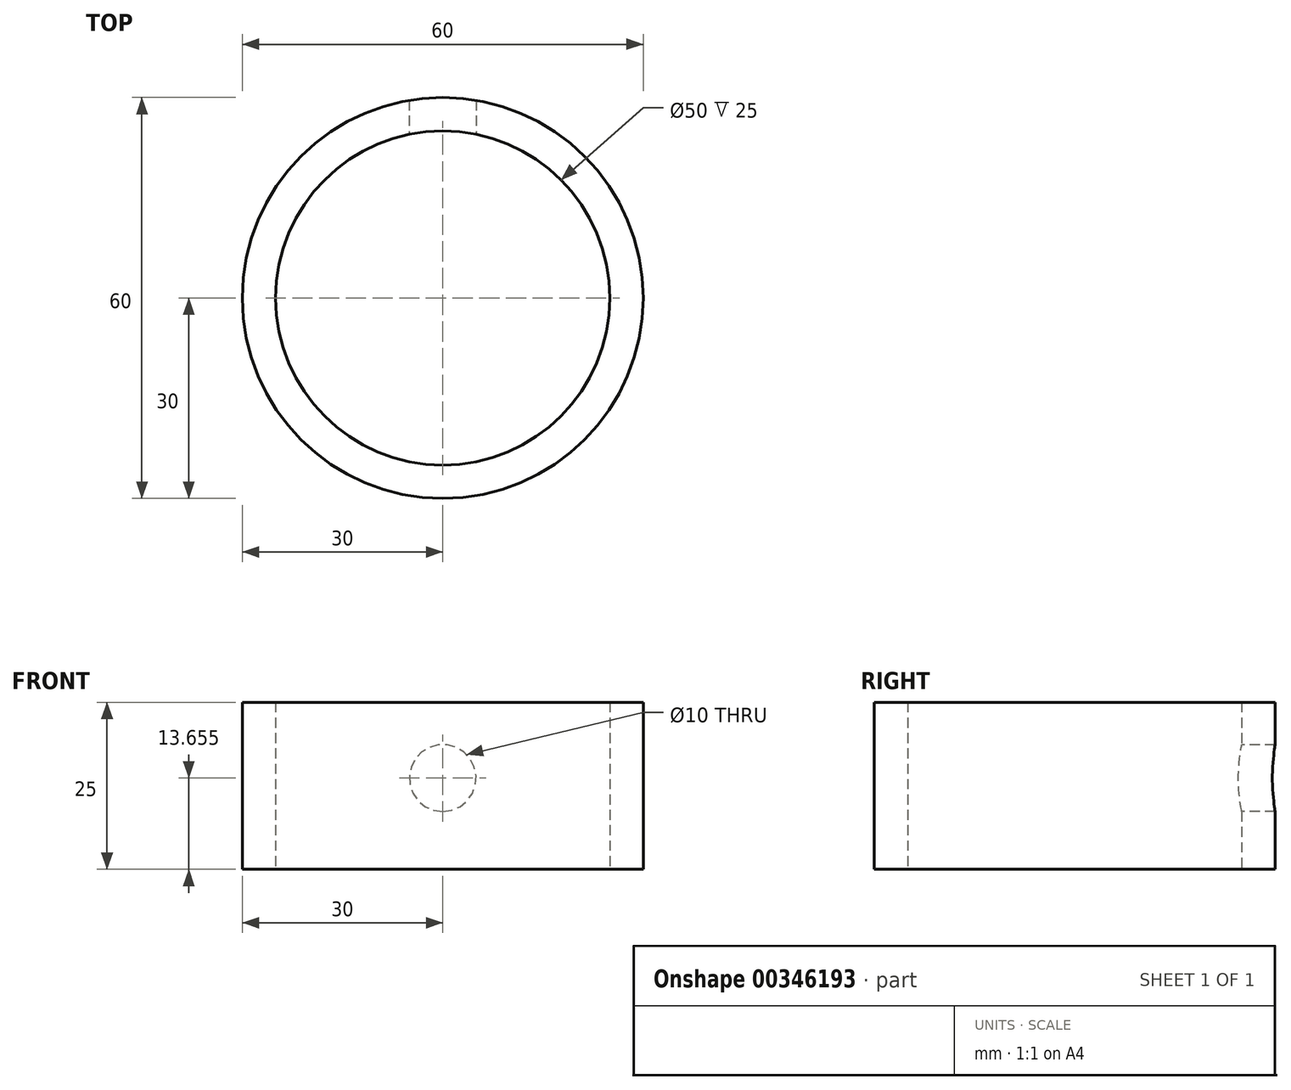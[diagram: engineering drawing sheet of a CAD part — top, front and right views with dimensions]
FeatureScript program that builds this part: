
annotation { "Feature Type Name" : "Feature", "Feature Type Description" : "" }
export const myFeature = defineFeature(function(context is Context, id is Id, definition is map)
    precondition{}
    {
        {
            var Q0;
            Q0=qCreatedBy(makeId("Top.planeOp"),FACE);
            var sketch = newSketch(context, id + "F0", { "sketchPlane" : qUnion([Q0])});
            skCircle(sketch, "E0", {"center": v(0, 0) * mm, "radius": 30 * mm});
            skCircle(sketch, "E1", {"center": v(0, 0) * mm, "radius": 25 * mm});
            skSolve(sketch);
        }
        {
            var Q0;
            Q0=makeQuery(id+"F0.imprint","IMPRINT",FACE,{"disambiguationData":[TD([[makeQuery(id+"F0.imprint","IMPRINT",EDGE,{"derivedFrom":sQuery(id+"F0.wireOp",EDGE,"E0")}),1.0]])]});
            extrude(context, id + "F1", {"entities" : qUnion([Q0]), "depth" : 25 * mm});
        }
        {
            var Q0;
            Q0=qCreatedBy(makeId("Front.planeOp"),FACE);
            var sketch = newSketch(context, id + "F2", { "sketchPlane" : qUnion([Q0])});
            skCircle(sketch, "E2", {"center": v(0, 13.65) * mm, "radius": 5 * mm});
            skSolve(sketch);
        }
        {
            var Q0;
            Q0 = qSketchRegion(id + "F2", true);
            extrude(context, id + "F3", {"entities" : qUnion([Q0]), "operationType" : NewBodyOperationType.REMOVE, "oppositeDirection" : true, "depth" : 50 * mm});
        }
    });
